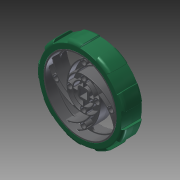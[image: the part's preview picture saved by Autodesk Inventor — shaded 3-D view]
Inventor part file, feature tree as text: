
AUTODESK INVENTOR PART (.ipt)
format: ipt  version: 2015 SP1 (Build 190203100, 203)  size: 9,245,184 bytes
history: native  units: in
note: dims shown in document units (in); Inventor stores cm internally (conversion verified against a paired STEP export)
features: other x2, imported_body x2, fillet x1
ambient origin geometry x8: Origin, YZ Plane, XZ Plane, XY Plane, X Axis, Y Axis, Z Axis, Center Point
bodies: Body1 (feature_tree), Body2 (feature_tree)
feature tree (5):
  other  "Wheel Medium"
  fillet  "Fillet42"  [1 undecoded]
  other  "_276-3525-001 Rev2_-_Chamfer1_"
  imported_body  "Base1"
  imported_body  "Base2"
note: 1 required parameter value undecoded (feature->parameter linkage not recoverable at this tier; creation-order binding heuristic only, values carry confidence <= 0.55)
